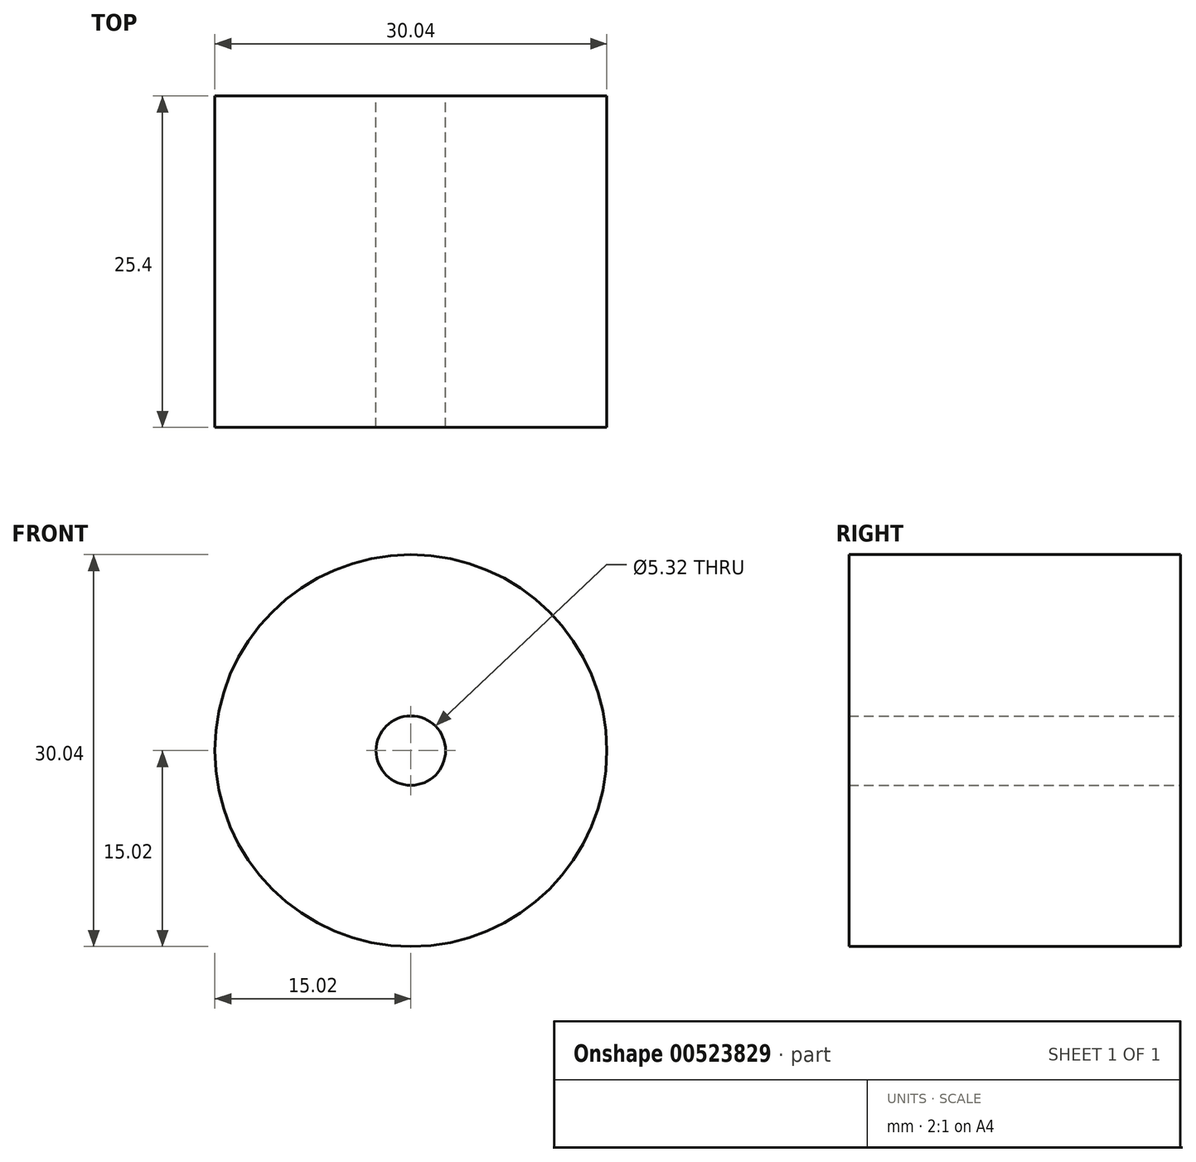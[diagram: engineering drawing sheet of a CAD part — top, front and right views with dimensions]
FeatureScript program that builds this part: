
annotation { "Feature Type Name" : "Feature", "Feature Type Description" : "" }
export const myFeature = defineFeature(function(context is Context, id is Id, definition is map)
    precondition{}
    {
        {
            var Q0;
            Q0=qCreatedBy(makeId("Front.planeOp"),FACE);
            var sketch = newSketch(context, id + "F0", { "sketchPlane" : qUnion([Q0])});
            skCircle(sketch, "E0", {"center": v(0, 0) * mm, "radius": 2.66 * mm});
            skCircle(sketch, "E1", {"center": v(0, 0) * mm, "radius": 8.67 * mm});
            skCircle(sketch, "E2.0", {"center": v(0, 0) * mm, "radius": 15.02 * mm});
            skSolve(sketch);
        }
        {
            var Q0;
            Q0 = qSketchRegion(id + "F0", true);
            var Q1;
            Q1=makeQuery(id+"F0.imprint","IMPRINT",FACE,{"disambiguationData":[TD([[makeQuery(id+"F0.imprint","IMPRINT",EDGE,{"derivedFrom":sQuery(id+"F0.wireOp",EDGE,"E0")}),-1.0]])]});
            extrude(context, id + "F1", {"entities" : qUnion([Q0, Q1]), "depth" : 25.4 * mm, "offsetDistance" : 25.4 * mm});
        }
    });
